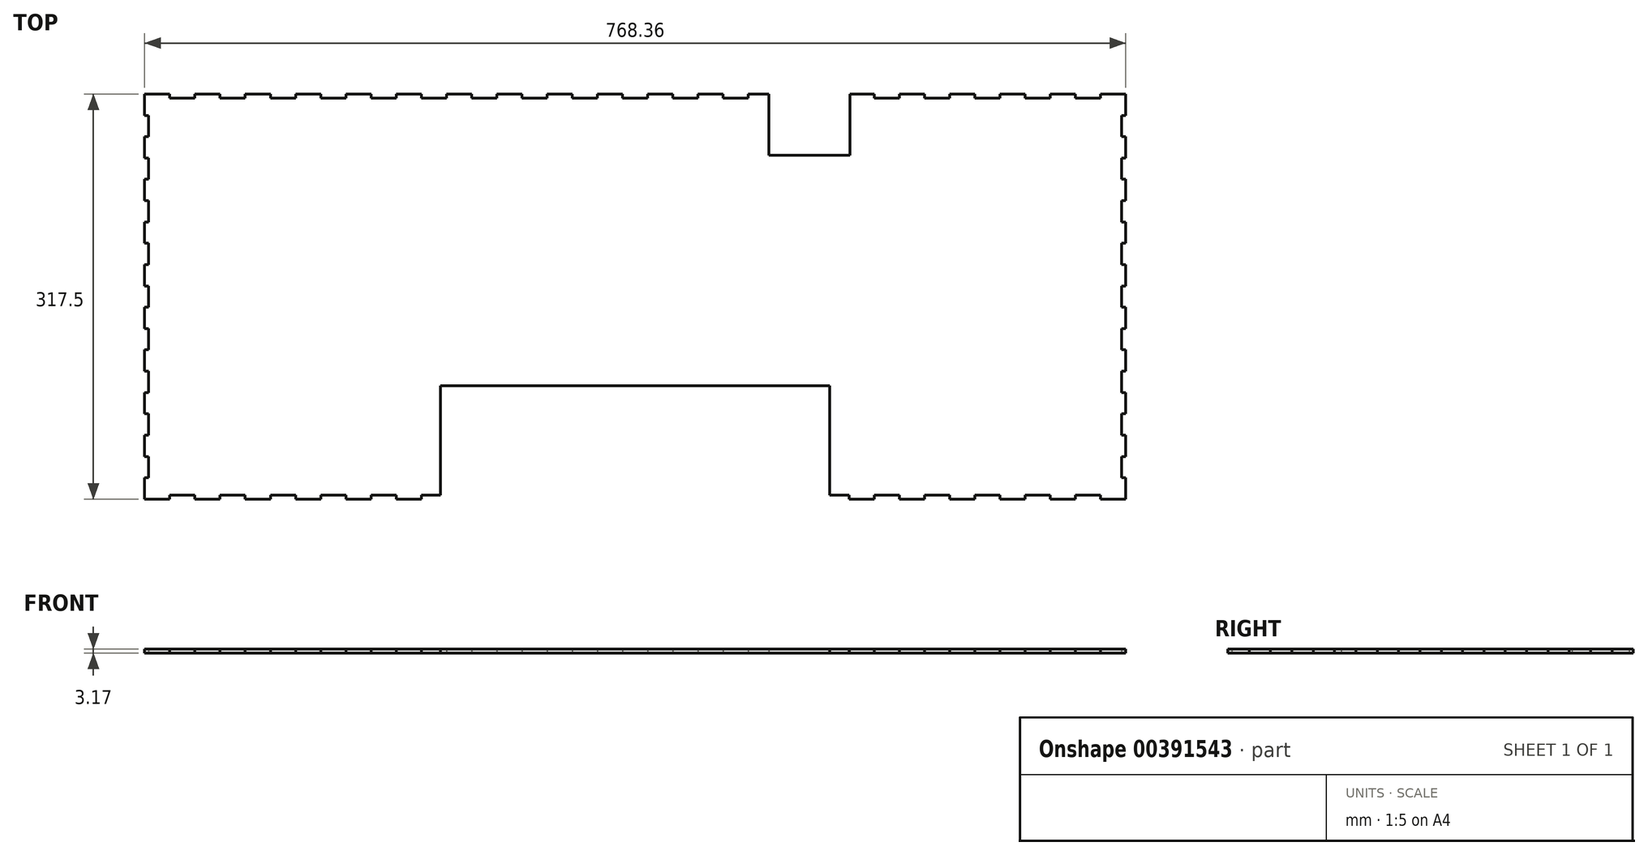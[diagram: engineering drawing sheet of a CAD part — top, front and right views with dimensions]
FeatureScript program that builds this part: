
annotation { "Feature Type Name" : "Feature", "Feature Type Description" : "" }
export const myFeature = defineFeature(function(context is Context, id is Id, definition is map)
    precondition{}
    {
        {
            var Q0;
            Q0=qCreatedBy(makeId("Top.planeOp"),FACE);
            var sketch = newSketch(context, id + "F0", { "sketchPlane" : qUnion([Q0])});
            skLineSegment(sketch, "E0.right", {"start": v(-384.18, -158.75) * mm, "end": v(-384.18, 158.75) * mm, "construction": true});
            skPoint(sketch, "E0.middle", {"position": v(0, 0) * mm});
            skLineSegment(sketch, "E1.bottom", {"start": v(-384.18, 158.75) * mm, "end": v(-364.47, 158.75) * mm});
            skLineSegment(sketch, "E1.left", {"start": v(-384.18, 158.75) * mm, "end": v(-384.18, 142.04) * mm});
            skLineSegment(sketch, "E2.right", {"start": v(-381, 142.04) * mm, "end": v(-381, 125.33) * mm});
            skLineSegment(sketch, "E3", {"start": v(-384.18, 142.04) * mm, "end": v(-381, 142.04) * mm});
            skLineSegment(sketch, "E4", {"start": v(-364.47, 158.75) * mm, "end": v(-364.47, 155.57) * mm});
            skLineSegment(sketch, "E5", {"start": v(-364.47, 155.57) * mm, "end": v(-344.77, 155.57) * mm});
            skLineSegment(sketch, "E6", {"start": v(384.18, 158.75) * mm, "end": v(-384.18, 158.75) * mm, "construction": true});
            skLineSegment(sketch, "E7", {"start": v(-381, 125.33) * mm, "end": v(-384.18, 125.33) * mm});
            skLineSegment(sketch, "E8.1.0.1", {"start": v(-384.18, 108.62) * mm, "end": v(-381, 108.62) * mm});
            skLineSegment(sketch, "E8.1.0.3", {"start": v(-384.17, 125.33) * mm, "end": v(-384.18, 108.62) * mm});
            skLineSegment(sketch, "E8.9.0.1", {"start": v(-384.17, -158.75) * mm, "end": v(-381, -158.75) * mm});
            skLineSegment(sketch, "E8.direction1", {"start": v(-384.18, 125.33) * mm, "end": v(-384.18, 91.9) * mm, "construction": true});
            skLineSegment(sketch, "E9", {"start": v(-344.77, 155.57) * mm, "end": v(-344.77, 158.75) * mm});
            skLineSegment(sketch, "E10.1.0.0", {"start": v(-325.07, 158.75) * mm, "end": v(-325.07, 155.58) * mm});
            skLineSegment(sketch, "E10.1.0.1", {"start": v(-325.07, 155.58) * mm, "end": v(-305.37, 155.58) * mm});
            skLineSegment(sketch, "E10.1.0.2", {"start": v(-305.37, 155.58) * mm, "end": v(-305.37, 158.75) * mm});
            skLineSegment(sketch, "E10.1.0.3", {"start": v(-344.77, 158.75) * mm, "end": v(-325.07, 158.75) * mm});
            skLineSegment(sketch, "E10.2.0.0", {"start": v(-285.67, 158.75) * mm, "end": v(-285.67, 155.58) * mm});
            skLineSegment(sketch, "E10.2.0.1", {"start": v(-285.67, 155.58) * mm, "end": v(-265.97, 155.58) * mm});
            skLineSegment(sketch, "E10.2.0.2", {"start": v(-265.97, 155.58) * mm, "end": v(-265.97, 158.75) * mm});
            skLineSegment(sketch, "E10.2.0.3", {"start": v(-305.37, 158.75) * mm, "end": v(-285.67, 158.75) * mm});
            skLineSegment(sketch, "E10.3.0.0", {"start": v(-246.27, 158.75) * mm, "end": v(-246.27, 155.58) * mm});
            skLineSegment(sketch, "E10.3.0.1", {"start": v(-246.27, 155.58) * mm, "end": v(-226.56, 155.58) * mm});
            skLineSegment(sketch, "E10.3.0.2", {"start": v(-226.56, 155.58) * mm, "end": v(-226.56, 158.75) * mm});
            skLineSegment(sketch, "E10.3.0.3", {"start": v(-265.97, 158.75) * mm, "end": v(-246.27, 158.75) * mm});
            skLineSegment(sketch, "E10.4.0.0", {"start": v(-206.86, 158.75) * mm, "end": v(-206.86, 155.58) * mm});
            skLineSegment(sketch, "E10.4.0.1", {"start": v(-206.86, 155.58) * mm, "end": v(-187.16, 155.58) * mm});
            skLineSegment(sketch, "E10.4.0.2", {"start": v(-187.16, 155.58) * mm, "end": v(-187.16, 158.75) * mm});
            skLineSegment(sketch, "E10.4.0.3", {"start": v(-226.56, 158.75) * mm, "end": v(-206.86, 158.75) * mm});
            skLineSegment(sketch, "E10.5.0.0", {"start": v(-167.46, 158.75) * mm, "end": v(-167.46, 155.58) * mm});
            skLineSegment(sketch, "E10.5.0.1", {"start": v(-167.46, 155.58) * mm, "end": v(-147.76, 155.58) * mm});
            skLineSegment(sketch, "E10.5.0.2", {"start": v(-147.76, 155.58) * mm, "end": v(-147.76, 158.75) * mm});
            skLineSegment(sketch, "E10.5.0.3", {"start": v(-187.16, 158.75) * mm, "end": v(-167.46, 158.75) * mm});
            skLineSegment(sketch, "E10.6.0.0", {"start": v(-128.06, 158.75) * mm, "end": v(-128.06, 155.58) * mm});
            skLineSegment(sketch, "E10.6.0.1", {"start": v(-128.06, 155.58) * mm, "end": v(-108.36, 155.58) * mm});
            skLineSegment(sketch, "E10.6.0.2", {"start": v(-108.36, 155.58) * mm, "end": v(-108.36, 158.75) * mm});
            skLineSegment(sketch, "E10.6.0.3", {"start": v(-147.76, 158.75) * mm, "end": v(-128.06, 158.75) * mm});
            skLineSegment(sketch, "E10.7.0.0", {"start": v(-88.66, 158.75) * mm, "end": v(-88.66, 155.58) * mm});
            skLineSegment(sketch, "E10.7.0.1", {"start": v(-88.66, 155.58) * mm, "end": v(-68.95, 155.58) * mm});
            skLineSegment(sketch, "E10.7.0.2", {"start": v(-68.95, 155.58) * mm, "end": v(-68.95, 158.75) * mm});
            skLineSegment(sketch, "E10.7.0.3", {"start": v(-108.36, 158.75) * mm, "end": v(-88.66, 158.75) * mm});
            skLineSegment(sketch, "E10.8.0.0", {"start": v(-49.25, 158.75) * mm, "end": v(-49.25, 155.58) * mm});
            skLineSegment(sketch, "E10.8.0.1", {"start": v(-49.25, 155.58) * mm, "end": v(-29.55, 155.58) * mm});
            skLineSegment(sketch, "E10.8.0.2", {"start": v(-29.55, 155.58) * mm, "end": v(-29.55, 158.75) * mm});
            skLineSegment(sketch, "E10.8.0.3", {"start": v(-68.95, 158.75) * mm, "end": v(-49.25, 158.75) * mm});
            skLineSegment(sketch, "E10.9.0.0", {"start": v(-9.85, 158.75) * mm, "end": v(-9.85, 155.58) * mm});
            skLineSegment(sketch, "E10.9.0.1", {"start": v(-9.85, 155.58) * mm, "end": v(9.85, 155.58) * mm});
            skLineSegment(sketch, "E10.9.0.2", {"start": v(9.85, 155.58) * mm, "end": v(9.85, 158.75) * mm});
            skLineSegment(sketch, "E10.9.0.3", {"start": v(-29.55, 158.75) * mm, "end": v(-9.85, 158.75) * mm});
            skLineSegment(sketch, "E10.10.0.0", {"start": v(29.55, 158.75) * mm, "end": v(29.55, 155.58) * mm});
            skLineSegment(sketch, "E10.10.0.1", {"start": v(29.55, 155.58) * mm, "end": v(49.25, 155.58) * mm});
            skLineSegment(sketch, "E10.10.0.2", {"start": v(49.25, 155.58) * mm, "end": v(49.25, 158.75) * mm});
            skLineSegment(sketch, "E10.10.0.3", {"start": v(9.85, 158.75) * mm, "end": v(29.55, 158.75) * mm});
            skLineSegment(sketch, "E10.11.0.0", {"start": v(68.95, 158.75) * mm, "end": v(68.95, 155.58) * mm});
            skLineSegment(sketch, "E10.11.0.1", {"start": v(68.95, 155.58) * mm, "end": v(88.66, 155.58) * mm});
            skLineSegment(sketch, "E10.11.0.2", {"start": v(88.66, 155.58) * mm, "end": v(88.66, 158.75) * mm});
            skLineSegment(sketch, "E10.11.0.3", {"start": v(49.25, 158.75) * mm, "end": v(68.95, 158.75) * mm});
            skLineSegment(sketch, "E10.12.0.0", {"start": v(108.36, 158.75) * mm, "end": v(108.36, 155.58) * mm});
            skLineSegment(sketch, "E10.12.0.3", {"start": v(88.66, 158.75) * mm, "end": v(108.36, 158.75) * mm});
            skLineSegment(sketch, "E10.16.0.2", {"start": v(285.67, 155.58) * mm, "end": v(285.67, 158.75) * mm});
            skLineSegment(sketch, "E10.17.0.0", {"start": v(305.37, 158.75) * mm, "end": v(305.37, 155.58) * mm});
            skLineSegment(sketch, "E10.17.0.1", {"start": v(305.37, 155.58) * mm, "end": v(325.07, 155.58) * mm});
            skLineSegment(sketch, "E10.17.0.2", {"start": v(325.07, 155.58) * mm, "end": v(325.07, 158.75) * mm});
            skLineSegment(sketch, "E10.17.0.3", {"start": v(285.67, 158.75) * mm, "end": v(305.37, 158.75) * mm});
            skLineSegment(sketch, "E10.18.0.0", {"start": v(344.77, 158.75) * mm, "end": v(344.77, 155.58) * mm});
            skLineSegment(sketch, "E10.18.0.1", {"start": v(344.77, 155.58) * mm, "end": v(364.47, 155.58) * mm});
            skLineSegment(sketch, "E10.18.0.2", {"start": v(364.47, 155.58) * mm, "end": v(364.47, 158.75) * mm});
            skLineSegment(sketch, "E10.18.0.3", {"start": v(325.07, 158.75) * mm, "end": v(344.77, 158.75) * mm});
            skLineSegment(sketch, "E10.19.0.3", {"start": v(364.47, 158.75) * mm, "end": v(384.18, 158.75) * mm});
            skLineSegment(sketch, "E10.direction1", {"start": v(-384.18, 158.75) * mm, "end": v(-344.77, 158.75) * mm, "construction": true});
            skLineSegment(sketch, "E11.MirrorCS", {"start": v(384.18, -158.75) * mm, "end": v(384.18, -155.58) * mm});
            skLineSegment(sketch, "E12.MirrorCS", {"start": v(-344.77, -155.57) * mm, "end": v(-344.77, -158.75) * mm});
            skLineSegment(sketch, "E13.MirrorCS", {"start": v(108.36, -158.75) * mm, "end": v(108.36, -155.58) * mm});
            skLineSegment(sketch, "E14.MirrorCS", {"start": v(285.67, -155.58) * mm, "end": v(285.67, -158.75) * mm});
            skLineSegment(sketch, "E15.MirrorCS", {"start": v(-285.67, -158.75) * mm, "end": v(-285.67, -155.58) * mm});
            skLineSegment(sketch, "E16.MirrorCS", {"start": v(49.25, -155.58) * mm, "end": v(49.25, -158.75) * mm});
            skLineSegment(sketch, "E17.MirrorCS", {"start": v(-108.36, -155.58) * mm, "end": v(-108.36, -158.75) * mm});
            skLineSegment(sketch, "E18.MirrorCS", {"start": v(-265.97, -155.58) * mm, "end": v(-265.97, -158.75) * mm});
            skLineSegment(sketch, "E19.MirrorCS", {"start": v(-29.55, -155.58) * mm, "end": v(-29.55, -158.75) * mm});
            skLineSegment(sketch, "E20.MirrorCS", {"start": v(364.47, -155.58) * mm, "end": v(364.47, -158.75) * mm});
            skLineSegment(sketch, "E21.MirrorCS", {"start": v(-206.86, -158.75) * mm, "end": v(-206.86, -155.58) * mm});
            skLineSegment(sketch, "E22.MirrorCS", {"start": v(-147.76, -155.58) * mm, "end": v(-147.76, -158.75) * mm});
            skLineSegment(sketch, "E23.MirrorCS", {"start": v(-305.37, -155.58) * mm, "end": v(-305.37, -158.75) * mm});
            skLineSegment(sketch, "E24.MirrorCS", {"start": v(206.86, -155.58) * mm, "end": v(206.86, -158.75) * mm});
            skLineSegment(sketch, "E25.MirrorCS", {"start": v(344.77, -158.75) * mm, "end": v(344.77, -155.58) * mm});
            skLineSegment(sketch, "E26.MirrorCS", {"start": v(128.06, -155.58) * mm, "end": v(128.06, -158.75) * mm});
            skLineSegment(sketch, "E27.MirrorCS", {"start": v(9.85, -155.58) * mm, "end": v(9.85, -158.75) * mm});
            skLineSegment(sketch, "E28.MirrorCS", {"start": v(-364.47, -158.75) * mm, "end": v(-364.47, -155.57) * mm});
            skLineSegment(sketch, "E29.MirrorCS", {"start": v(325.07, -155.58) * mm, "end": v(325.07, -158.75) * mm});
            skLineSegment(sketch, "E30.MirrorCS", {"start": v(167.46, -155.58) * mm, "end": v(167.46, -158.75) * mm});
            skLineSegment(sketch, "E31.MirrorCS", {"start": v(147.76, -158.75) * mm, "end": v(147.76, -155.58) * mm});
            skLineSegment(sketch, "E32.MirrorCS", {"start": v(305.37, -158.75) * mm, "end": v(305.37, -155.58) * mm});
            skLineSegment(sketch, "E33.MirrorCS", {"start": v(-88.66, -158.75) * mm, "end": v(-88.66, -155.58) * mm});
            skLineSegment(sketch, "E34.MirrorCS", {"start": v(29.55, -158.75) * mm, "end": v(29.55, -155.58) * mm});
            skLineSegment(sketch, "E35.MirrorCS", {"start": v(-128.06, -158.75) * mm, "end": v(-128.06, -155.58) * mm});
            skLineSegment(sketch, "E36.MirrorCS", {"start": v(-226.56, -155.58) * mm, "end": v(-226.56, -158.75) * mm});
            skLineSegment(sketch, "E37.MirrorCS", {"start": v(88.66, -155.58) * mm, "end": v(88.66, -158.75) * mm});
            skLineSegment(sketch, "E38.MirrorCS", {"start": v(246.27, -155.58) * mm, "end": v(246.27, -158.75) * mm});
            skLineSegment(sketch, "E39.MirrorCS", {"start": v(-68.95, -155.58) * mm, "end": v(-68.95, -158.75) * mm});
            skLineSegment(sketch, "E40.MirrorCS", {"start": v(265.97, -158.75) * mm, "end": v(265.97, -155.58) * mm});
            skLineSegment(sketch, "E41.MirrorCS", {"start": v(-325.07, -158.75) * mm, "end": v(-325.07, -155.58) * mm});
            skLineSegment(sketch, "E42.MirrorCS", {"start": v(187.16, -158.75) * mm, "end": v(187.16, -155.58) * mm});
            skLineSegment(sketch, "E43.MirrorCS", {"start": v(-187.16, -155.58) * mm, "end": v(-187.16, -158.75) * mm});
            skLineSegment(sketch, "E44.MirrorCS", {"start": v(-167.46, -158.75) * mm, "end": v(-167.46, -155.58) * mm});
            skLineSegment(sketch, "E45.MirrorCS", {"start": v(-9.85, -158.75) * mm, "end": v(-9.85, -155.58) * mm});
            skLineSegment(sketch, "E46.MirrorCS", {"start": v(-246.27, -158.75) * mm, "end": v(-246.27, -155.58) * mm});
            skLineSegment(sketch, "E47.MirrorCS", {"start": v(226.56, -158.75) * mm, "end": v(226.56, -155.58) * mm});
            skLineSegment(sketch, "E48.MirrorCS", {"start": v(68.95, -158.75) * mm, "end": v(68.95, -155.58) * mm});
            skLineSegment(sketch, "E49.MirrorCS", {"start": v(-49.25, -158.75) * mm, "end": v(-49.25, -155.58) * mm});
            skLineSegment(sketch, "E50.MirrorCS", {"start": v(-68.95, -158.75) * mm, "end": v(-49.25, -158.75) * mm});
            skLineSegment(sketch, "E51.MirrorCS", {"start": v(-226.56, -158.75) * mm, "end": v(-206.86, -158.75) * mm});
            skLineSegment(sketch, "E52.MirrorCS", {"start": v(246.27, -158.75) * mm, "end": v(265.97, -158.75) * mm});
            skLineSegment(sketch, "E53.MirrorCS", {"start": v(206.86, -158.75) * mm, "end": v(226.56, -158.75) * mm});
            skLineSegment(sketch, "E54.MirrorCS", {"start": v(49.25, -158.75) * mm, "end": v(68.95, -158.75) * mm});
            skLineSegment(sketch, "E55.MirrorCS", {"start": v(-265.97, -158.75) * mm, "end": v(-246.27, -158.75) * mm});
            skLineSegment(sketch, "E56.MirrorCS", {"start": v(-108.36, -158.75) * mm, "end": v(-88.66, -158.75) * mm});
            skLineSegment(sketch, "E57.MirrorCS", {"start": v(88.66, -158.75) * mm, "end": v(108.36, -158.75) * mm});
            skLineSegment(sketch, "E58.MirrorCS", {"start": v(-344.77, -158.75) * mm, "end": v(-325.07, -158.75) * mm});
            skLineSegment(sketch, "E59.MirrorCS", {"start": v(285.67, -158.75) * mm, "end": v(305.37, -158.75) * mm});
            skLineSegment(sketch, "E60.MirrorCS", {"start": v(128.06, -158.75) * mm, "end": v(147.76, -158.75) * mm});
            skLineSegment(sketch, "E61.MirrorCS", {"start": v(-384.18, -158.75) * mm, "end": v(-364.47, -158.75) * mm});
            skLineSegment(sketch, "E62.MirrorCS", {"start": v(167.46, -158.75) * mm, "end": v(187.16, -158.75) * mm});
            skLineSegment(sketch, "E63.MirrorCS", {"start": v(325.07, -158.75) * mm, "end": v(344.77, -158.75) * mm});
            skLineSegment(sketch, "E64.MirrorCS", {"start": v(364.47, -158.75) * mm, "end": v(384.18, -158.75) * mm});
            skLineSegment(sketch, "E65.MirrorCS", {"start": v(-29.55, -158.75) * mm, "end": v(-9.85, -158.75) * mm});
            skLineSegment(sketch, "E66.MirrorCS", {"start": v(-187.16, -158.75) * mm, "end": v(-167.46, -158.75) * mm});
            skLineSegment(sketch, "E67.MirrorCS", {"start": v(-305.37, -158.75) * mm, "end": v(-285.67, -158.75) * mm});
            skLineSegment(sketch, "E68.MirrorCS", {"start": v(-147.76, -158.75) * mm, "end": v(-128.06, -158.75) * mm});
            skLineSegment(sketch, "E69.MirrorCS", {"start": v(9.85, -158.75) * mm, "end": v(29.55, -158.75) * mm});
            skLineSegment(sketch, "E70.MirrorCS", {"start": v(29.55, -155.58) * mm, "end": v(49.25, -155.58) * mm});
            skLineSegment(sketch, "E71.MirrorCS", {"start": v(226.56, -155.58) * mm, "end": v(246.27, -155.58) * mm});
            skLineSegment(sketch, "E72.MirrorCS", {"start": v(-88.66, -155.58) * mm, "end": v(-68.95, -155.58) * mm});
            skLineSegment(sketch, "E73.MirrorCS", {"start": v(-49.25, -155.58) * mm, "end": v(-29.55, -155.58) * mm});
            skLineSegment(sketch, "E74.MirrorCS", {"start": v(-206.86, -155.58) * mm, "end": v(-187.16, -155.58) * mm});
            skLineSegment(sketch, "E75.MirrorCS", {"start": v(-364.47, -155.57) * mm, "end": v(-344.77, -155.57) * mm});
            skLineSegment(sketch, "E76.MirrorCS", {"start": v(384.18, -158.75) * mm, "end": v(-384.18, -158.75) * mm, "construction": true});
            skLineSegment(sketch, "E77.MirrorCS", {"start": v(-128.06, -155.58) * mm, "end": v(-108.36, -155.58) * mm});
            skLineSegment(sketch, "E78.MirrorCS", {"start": v(-285.67, -155.58) * mm, "end": v(-265.97, -155.58) * mm});
            skLineSegment(sketch, "E79.MirrorCS", {"start": v(344.77, -155.58) * mm, "end": v(364.47, -155.58) * mm});
            skLineSegment(sketch, "E80.MirrorCS", {"start": v(-9.85, -155.58) * mm, "end": v(9.85, -155.58) * mm});
            skLineSegment(sketch, "E81.MirrorCS", {"start": v(-167.46, -155.58) * mm, "end": v(-147.76, -155.58) * mm});
            skLineSegment(sketch, "E82.MirrorCS", {"start": v(-325.07, -155.58) * mm, "end": v(-305.37, -155.58) * mm});
            skLineSegment(sketch, "E83.MirrorCS", {"start": v(305.37, -155.58) * mm, "end": v(325.07, -155.58) * mm});
            skLineSegment(sketch, "E84.MirrorCS", {"start": v(147.76, -155.58) * mm, "end": v(167.46, -155.58) * mm});
            skLineSegment(sketch, "E85.MirrorCS", {"start": v(265.97, -155.58) * mm, "end": v(285.67, -155.58) * mm});
            skLineSegment(sketch, "E86.MirrorCS", {"start": v(-246.27, -155.58) * mm, "end": v(-226.56, -155.58) * mm});
            skLineSegment(sketch, "E87.MirrorCS", {"start": v(68.95, -155.58) * mm, "end": v(88.66, -155.58) * mm});
            skLineSegment(sketch, "E88.MirrorCS", {"start": v(187.16, -155.58) * mm, "end": v(206.86, -155.58) * mm});
            skLineSegment(sketch, "E89.MirrorCS", {"start": v(-384.18, -158.75) * mm, "end": v(-344.77, -158.75) * mm, "construction": true});
            skLineSegment(sketch, "E90.MirrorCS", {"start": v(108.36, -155.58) * mm, "end": v(128.06, -155.58) * mm});
            skLineSegment(sketch, "E91.MirrorCS", {"start": v(384.17, -158.75) * mm, "end": v(381, -158.75) * mm});
            skLineSegment(sketch, "E92.MirrorCS", {"start": v(384.18, -158.75) * mm, "end": v(384.18, 158.75) * mm, "construction": true});
            skLineSegment(sketch, "E93", {"start": v(104.78, 110.81) * mm, "end": v(104.78, 136.48) * mm, "construction": true});
            skLineSegment(sketch, "E94", {"start": v(168.28, 138.21) * mm, "end": v(168.28, 115.73) * mm, "construction": true});
            skLineSegment(sketch, "E95", {"start": v(108.36, 155.58) * mm, "end": v(111.13, 155.58) * mm});
            skLineSegment(sketch, "E96", {"start": v(285.67, 155.58) * mm, "end": v(268.6, 155.58) * mm});
            skLineSegment(sketch, "E97.MirrorCS", {"start": v(167.46, 155.58) * mm, "end": v(167.46, 158.75) * mm});
            skLineSegment(sketch, "E98.MirrorCS", {"start": v(147.76, 158.75) * mm, "end": v(147.76, 155.58) * mm});
            skLineSegment(sketch, "E99.MirrorCS", {"start": v(128.06, 155.58) * mm, "end": v(128.06, 158.75) * mm});
            skLineSegment(sketch, "E100.MirrorCS", {"start": v(265.97, 158.75) * mm, "end": v(265.97, 155.58) * mm});
            skLineSegment(sketch, "E101.MirrorCS", {"start": v(246.27, 155.58) * mm, "end": v(246.27, 158.75) * mm});
            skLineSegment(sketch, "E102.MirrorCS", {"start": v(226.56, 158.75) * mm, "end": v(226.56, 155.58) * mm});
            skLineSegment(sketch, "E103.MirrorCS", {"start": v(187.16, 158.75) * mm, "end": v(187.16, 155.58) * mm});
            skLineSegment(sketch, "E104.MirrorCS", {"start": v(206.86, 155.58) * mm, "end": v(206.86, 158.75) * mm});
            skLineSegment(sketch, "E105.MirrorCS", {"start": v(265.97, 155.58) * mm, "end": v(285.67, 155.58) * mm});
            skLineSegment(sketch, "E106.MirrorCS", {"start": v(206.86, 158.75) * mm, "end": v(226.56, 158.75) * mm});
            skLineSegment(sketch, "E107.MirrorCS", {"start": v(147.76, 155.58) * mm, "end": v(167.46, 155.58) * mm});
            skLineSegment(sketch, "E108.MirrorCS", {"start": v(246.27, 158.75) * mm, "end": v(265.97, 158.75) * mm});
            skLineSegment(sketch, "E109.MirrorCS", {"start": v(167.46, 158.75) * mm, "end": v(187.16, 158.75) * mm});
            skLineSegment(sketch, "E110.MirrorCS", {"start": v(128.06, 158.75) * mm, "end": v(147.76, 158.75) * mm});
            skLineSegment(sketch, "E111.MirrorCS", {"start": v(108.36, 155.58) * mm, "end": v(128.06, 155.58) * mm});
            skLineSegment(sketch, "E112.MirrorCS", {"start": v(187.16, 155.58) * mm, "end": v(206.86, 155.58) * mm});
            skLineSegment(sketch, "E113.MirrorCS", {"start": v(226.56, 155.58) * mm, "end": v(246.27, 155.58) * mm});
            skLineSegment(sketch, "E114", {"start": v(168.28, 138.21) * mm, "end": v(168.28, 188.5) * mm, "construction": true});
            skLineSegment(sketch, "E115.bottom", {"start": v(104.78, 110.81) * mm, "end": v(168.28, 110.81) * mm});
            skLineSegment(sketch, "E115.top", {"start": v(104.78, 188.5) * mm, "end": v(168.28, 188.5) * mm});
            skLineSegment(sketch, "E115.left", {"start": v(104.78, 110.81) * mm, "end": v(104.77, 188.5) * mm});
            skLineSegment(sketch, "E115.right", {"start": v(168.28, 110.81) * mm, "end": v(168.28, 188.5) * mm});
            skLineSegment(sketch, "E116.1.0.1", {"start": v(-381, 108.62) * mm, "end": v(-381, 91.9) * mm});
            skLineSegment(sketch, "E116.1.0.3", {"start": v(-381, 91.9) * mm, "end": v(-384.18, 91.9) * mm});
            skLineSegment(sketch, "E116.2.0.0", {"start": v(-384.17, 91.9) * mm, "end": v(-384.17, 75.2) * mm});
            skLineSegment(sketch, "E116.2.0.1", {"start": v(-381, 75.2) * mm, "end": v(-381, 58.49) * mm});
            skLineSegment(sketch, "E116.2.0.2", {"start": v(-384.18, 75.2) * mm, "end": v(-381, 75.2) * mm});
            skLineSegment(sketch, "E116.2.0.3", {"start": v(-381, 58.49) * mm, "end": v(-384.17, 58.49) * mm});
            skLineSegment(sketch, "E116.3.0.0", {"start": v(-384.17, 58.49) * mm, "end": v(-384.17, 41.78) * mm});
            skLineSegment(sketch, "E116.3.0.1", {"start": v(-381, 41.78) * mm, "end": v(-381, 25.07) * mm});
            skLineSegment(sketch, "E116.3.0.2", {"start": v(-384.17, 41.78) * mm, "end": v(-381, 41.78) * mm});
            skLineSegment(sketch, "E116.3.0.3", {"start": v(-381, 25.07) * mm, "end": v(-384.17, 25.07) * mm});
            skLineSegment(sketch, "E116.4.0.0", {"start": v(-384.17, 25.07) * mm, "end": v(-384.17, 8.36) * mm});
            skLineSegment(sketch, "E116.4.0.1", {"start": v(-381, 8.36) * mm, "end": v(-381, -8.36) * mm});
            skLineSegment(sketch, "E116.4.0.2", {"start": v(-384.17, 8.36) * mm, "end": v(-381, 8.36) * mm});
            skLineSegment(sketch, "E116.4.0.3", {"start": v(-381, -8.36) * mm, "end": v(-384.17, -8.36) * mm});
            skLineSegment(sketch, "E116.5.0.0", {"start": v(-384.17, -8.36) * mm, "end": v(-384.17, -25.07) * mm});
            skLineSegment(sketch, "E116.5.0.1", {"start": v(-381, -25.07) * mm, "end": v(-381, -41.78) * mm});
            skLineSegment(sketch, "E116.5.0.2", {"start": v(-384.17, -25.07) * mm, "end": v(-381, -25.07) * mm});
            skLineSegment(sketch, "E116.5.0.3", {"start": v(-381, -41.78) * mm, "end": v(-384.17, -41.78) * mm});
            skLineSegment(sketch, "E116.6.0.0", {"start": v(-384.17, -41.78) * mm, "end": v(-384.17, -58.49) * mm});
            skLineSegment(sketch, "E116.6.0.1", {"start": v(-381, -58.49) * mm, "end": v(-381, -75.2) * mm});
            skLineSegment(sketch, "E116.6.0.2", {"start": v(-384.17, -58.49) * mm, "end": v(-381, -58.49) * mm});
            skLineSegment(sketch, "E116.6.0.3", {"start": v(-381, -75.2) * mm, "end": v(-384.17, -75.2) * mm});
            skLineSegment(sketch, "E116.7.0.0", {"start": v(-384.17, -75.2) * mm, "end": v(-384.17, -91.9) * mm});
            skLineSegment(sketch, "E116.7.0.1", {"start": v(-381, -91.9) * mm, "end": v(-381, -108.62) * mm});
            skLineSegment(sketch, "E116.7.0.2", {"start": v(-384.17, -91.9) * mm, "end": v(-381, -91.9) * mm});
            skLineSegment(sketch, "E116.7.0.3", {"start": v(-381, -108.62) * mm, "end": v(-384.17, -108.62) * mm});
            skLineSegment(sketch, "E116.8.0.0", {"start": v(-384.17, -108.62) * mm, "end": v(-384.17, -125.33) * mm});
            skLineSegment(sketch, "E116.8.0.1", {"start": v(-381, -125.33) * mm, "end": v(-381, -142.04) * mm});
            skLineSegment(sketch, "E116.8.0.2", {"start": v(-384.17, -125.33) * mm, "end": v(-381, -125.33) * mm});
            skLineSegment(sketch, "E116.8.0.3", {"start": v(-381, -142.04) * mm, "end": v(-384.17, -142.04) * mm});
            skLineSegment(sketch, "E116.9.0.0", {"start": v(-384.17, -142.04) * mm, "end": v(-384.17, -158.75) * mm});
            skLineSegment(sketch, "E117", {"start": v(-384.18, 125.33) * mm, "end": v(-384.18, 108.62) * mm});
            skLineSegment(sketch, "E118", {"start": v(-384.18, 91.9) * mm, "end": v(-384.18, 75.2) * mm});
            skLineSegment(sketch, "E119.MirrorCS", {"start": v(384.18, 108.62) * mm, "end": v(381, 108.62) * mm});
            skLineSegment(sketch, "E120.MirrorCS", {"start": v(384.17, 125.33) * mm, "end": v(384.18, 108.62) * mm});
            skLineSegment(sketch, "E121.MirrorCS", {"start": v(384.18, 125.33) * mm, "end": v(384.18, 108.62) * mm});
            skLineSegment(sketch, "E122.MirrorCS", {"start": v(381, 91.9) * mm, "end": v(384.18, 91.9) * mm});
            skLineSegment(sketch, "E123.MirrorCS", {"start": v(381, 125.33) * mm, "end": v(384.18, 125.33) * mm});
            skLineSegment(sketch, "E124.MirrorCS", {"start": v(384.17, -142.04) * mm, "end": v(384.17, -158.75) * mm});
            skLineSegment(sketch, "E125.MirrorCS", {"start": v(381, 58.49) * mm, "end": v(384.17, 58.49) * mm});
            skLineSegment(sketch, "E126.MirrorCS", {"start": v(381, -142.04) * mm, "end": v(384.17, -142.04) * mm});
            skLineSegment(sketch, "E127.MirrorCS", {"start": v(384.18, 91.9) * mm, "end": v(384.18, 75.2) * mm});
            skLineSegment(sketch, "E128.MirrorCS", {"start": v(381, -41.78) * mm, "end": v(384.17, -41.78) * mm});
            skLineSegment(sketch, "E129.MirrorCS", {"start": v(381, -8.36) * mm, "end": v(384.17, -8.36) * mm});
            skLineSegment(sketch, "E130.MirrorCS", {"start": v(381, 25.07) * mm, "end": v(384.17, 25.07) * mm});
            skLineSegment(sketch, "E131.MirrorCS", {"start": v(381, -108.62) * mm, "end": v(384.17, -108.62) * mm});
            skLineSegment(sketch, "E132.MirrorCS", {"start": v(381, -75.2) * mm, "end": v(384.17, -75.2) * mm});
            skLineSegment(sketch, "E133.MirrorCS", {"start": v(384.18, 75.2) * mm, "end": v(381, 75.2) * mm});
            skLineSegment(sketch, "E134.MirrorCS", {"start": v(384.17, 91.9) * mm, "end": v(384.17, 75.2) * mm});
            skLineSegment(sketch, "E135.MirrorCS", {"start": v(384.18, 142.04) * mm, "end": v(381, 142.04) * mm});
            skLineSegment(sketch, "E136.MirrorCS", {"start": v(384.17, 58.49) * mm, "end": v(384.17, 41.78) * mm});
            skLineSegment(sketch, "E137.MirrorCS", {"start": v(384.17, -58.49) * mm, "end": v(381, -58.49) * mm});
            skLineSegment(sketch, "E138.MirrorCS", {"start": v(381, -58.49) * mm, "end": v(381, -75.2) * mm});
            skLineSegment(sketch, "E139.MirrorCS", {"start": v(384.17, -25.07) * mm, "end": v(381, -25.07) * mm});
            skLineSegment(sketch, "E140.MirrorCS", {"start": v(381, -25.07) * mm, "end": v(381, -41.78) * mm});
            skLineSegment(sketch, "E141.MirrorCS", {"start": v(384.17, 8.36) * mm, "end": v(381, 8.36) * mm});
            skLineSegment(sketch, "E142.MirrorCS", {"start": v(384.17, -125.33) * mm, "end": v(381, -125.33) * mm});
            skLineSegment(sketch, "E143.MirrorCS", {"start": v(384.17, -108.62) * mm, "end": v(384.17, -125.33) * mm});
            skLineSegment(sketch, "E144.MirrorCS", {"start": v(384.17, 41.78) * mm, "end": v(381, 41.78) * mm});
            skLineSegment(sketch, "E145.MirrorCS", {"start": v(384.17, -91.9) * mm, "end": v(381, -91.9) * mm});
            skLineSegment(sketch, "E146.MirrorCS", {"start": v(381, 8.36) * mm, "end": v(381, -8.36) * mm});
            skLineSegment(sketch, "E147.MirrorCS", {"start": v(384.18, 158.75) * mm, "end": v(384.18, 142.04) * mm});
            skLineSegment(sketch, "E148.MirrorCS", {"start": v(384.17, -41.78) * mm, "end": v(384.17, -58.49) * mm});
            skLineSegment(sketch, "E149.MirrorCS", {"start": v(384.17, 25.07) * mm, "end": v(384.17, 8.36) * mm});
            skLineSegment(sketch, "E150.MirrorCS", {"start": v(384.17, -8.36) * mm, "end": v(384.17, -25.07) * mm});
            skLineSegment(sketch, "E151.MirrorCS", {"start": v(384.17, -75.2) * mm, "end": v(384.17, -91.9) * mm});
            skLineSegment(sketch, "E152.MirrorCS", {"start": v(384.18, 125.33) * mm, "end": v(384.18, 91.9) * mm, "construction": true});
            skLineSegment(sketch, "E153.MirrorCS", {"start": v(381, 142.04) * mm, "end": v(381, 125.33) * mm});
            skLineSegment(sketch, "E154.MirrorCS", {"start": v(381, 41.78) * mm, "end": v(381, 25.07) * mm});
            skLineSegment(sketch, "E155.MirrorCS", {"start": v(381, -91.9) * mm, "end": v(381, -108.62) * mm});
            skLineSegment(sketch, "E156.MirrorCS", {"start": v(381, 75.2) * mm, "end": v(381, 58.49) * mm});
            skLineSegment(sketch, "E157.MirrorCS", {"start": v(381, 108.62) * mm, "end": v(381, 91.9) * mm});
            skLineSegment(sketch, "E158.MirrorCS", {"start": v(381, -125.33) * mm, "end": v(381, -142.04) * mm});
            skLineSegment(sketch, "E159.bottom", {"start": v(-152.4, -233.88) * mm, "end": v(152.4, -233.88) * mm});
            skLineSegment(sketch, "E159.top", {"start": v(-152.4, -69.85) * mm, "end": v(152.4, -69.85) * mm});
            skLineSegment(sketch, "E159.left", {"start": v(-152.4, -233.88) * mm, "end": v(-152.4, -69.85) * mm});
            skLineSegment(sketch, "E159.right", {"start": v(152.4, -233.88) * mm, "end": v(152.4, -69.85) * mm});
            skSolve(sketch);
        }
        {
            var Q0;
            Q0=makeQuery(id+"F0.imprint","IMPRINT",FACE,{"disambiguationData":[TD([[makeQuery(id+"F0.imprint","IMPRINT",EDGE,{"derivedFrom":sQuery(id+"F0.wireOp",EDGE,"E10.17.0.0")}),-1.0]])]});
            var Q1;
            Q1=makeQuery(id+"F0.imprint","IMPRINT",FACE,{"disambiguationData":[TD([[makeQuery(id+"F0.imprint","IMPRINT",EDGE,{"derivedFrom":sQuery(id+"F0.wireOp",EDGE,"E1.bottom")}),-1.0]])]});
            var Q2;
            Q2=makeQuery(id+"F0.imprint","IMPRINT",FACE,{"disambiguationData":[TD([[makeQuery(id+"F0.imprint","IMPRINT",EDGE,{"derivedFrom":sQuery(id+"F0.wireOp",EDGE,"E8.4.0.0")}),1.0]])]});
            var Q3;
            Q3=makeQuery(id+"F0.imprint","IMPRINT",FACE,{"disambiguationData":[TD([[makeQuery(id+"F0.imprint","IMPRINT",EDGE,{"derivedFrom":sQuery(id+"F0.wireOp",EDGE,"E8.7.0.0")}),1.0]])]});
            var Q4;
            Q4=makeQuery(id+"F0.imprint","IMPRINT",FACE,{"disambiguationData":[TD([[makeQuery(id+"F0.imprint","IMPRINT",EDGE,{"derivedFrom":sQuery(id+"F0.wireOp",EDGE,"a2fb0b88-96b9-4597-90f2-df873ef2a7f114.MirrorCS")}),-1.0]])]});
            extrude(context, id + "F1", {"entities" : qUnion([Q0, Q1, Q2, Q3, Q4]), "depth" : 3.17 * mm});
        }
    });
